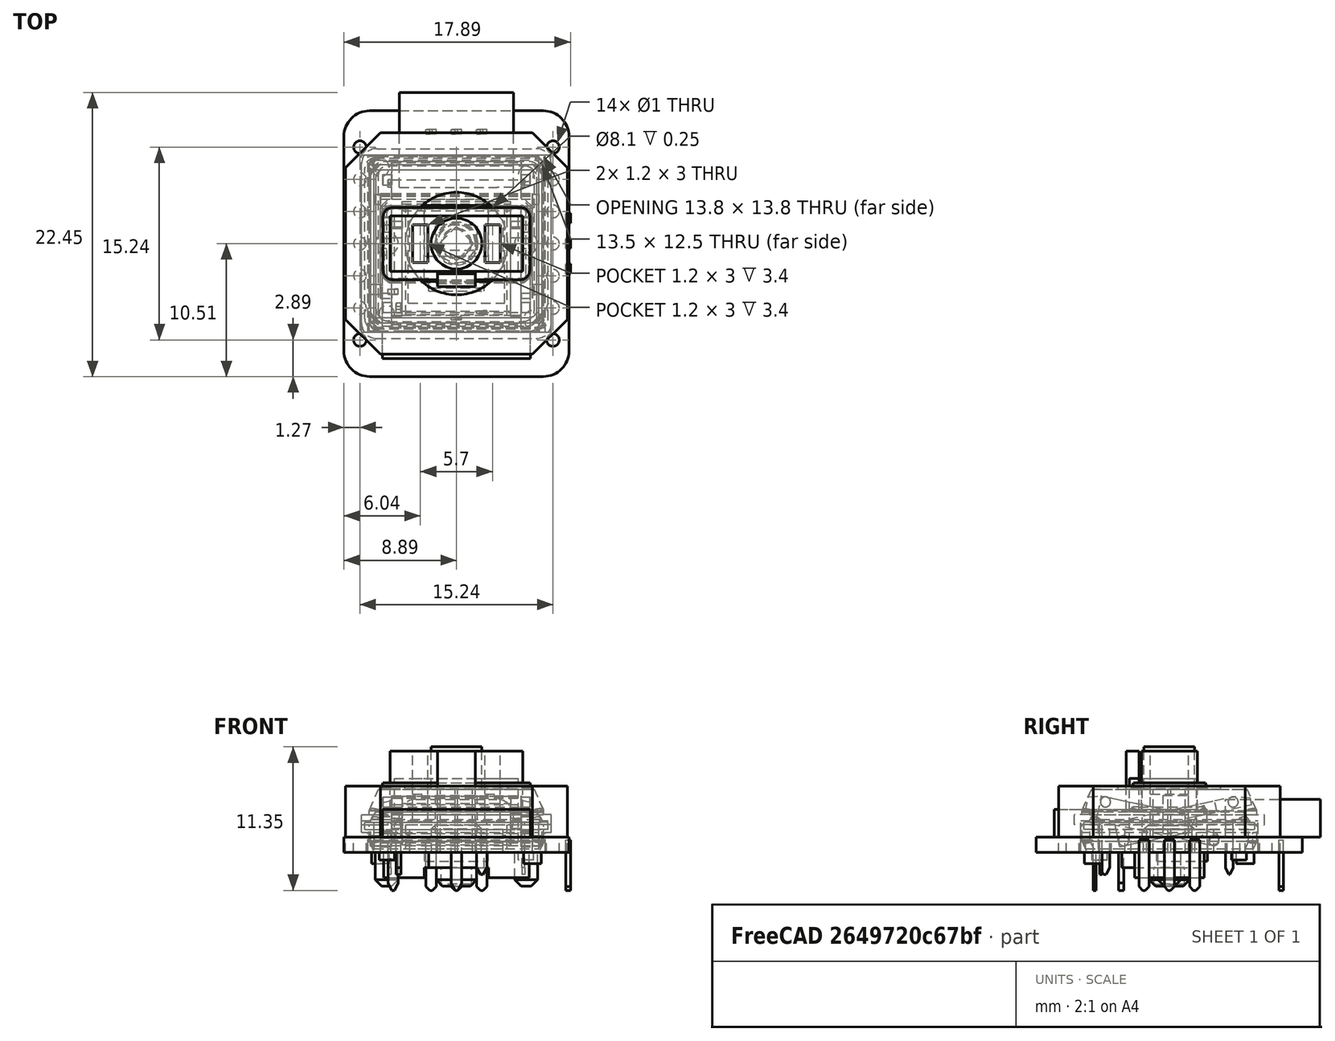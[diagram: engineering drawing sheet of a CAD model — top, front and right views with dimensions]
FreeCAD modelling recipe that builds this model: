
FCSTD DOCUMENT  (FreeCAD 0.18R)
Label: Keyboard
License: All rights reserved
LicenseURL: http://en.wikipedia.org/wiki/All_rights_reserved
objects: Part::Box×59, Part::Chamfer×31, Part::Cylinder×21, Part::MultiFuse×14, Part::Fillet×9, App::DocumentObjectGroup×6, Part::Cut×4, Part::FeaturePython×3
note: 141 computed .brp shape members not serialized (recipe doc carries the construction recipe); baked Part::Feature solids carry a one-line shape summary decoded from their .brp

FEATURE [Part::Box] Box  label="JT8P_Base"
  AttacherType = Attacher::AttachEngine3D
  Height = 5.25
  Length = 17.5
  Placement = pos=(-8.75,-8.75,0) rot=(0,0,1;0rad)
  Width = 17.5
FEATURE [Part::Cylinder] Cylinder  label="JT8P_TopHole"
  Angle = 360
  AttacherType = Attacher::AttachEngine3D
  Height = 2
  Placement = pos=(0,0,5) rot=(0,0,1;0rad)
  Radius = 4.05
FEATURE [Part::Cylinder] Cylinder001  label="JT8P_knob"
  Angle = 360
  AttacherType = Attacher::AttachEngine3D
  Height = 3.35
  Placement = pos=(0,0,5) rot=(0,0,1;0rad)
  Radius = 2
FEATURE [Part::Cylinder] Cylinder002  label="JT8P_Leg1"
  Angle = 360
  AttacherType = Attacher::AttachEngine3D
  Height = 0.9
  Placement = pos=(-6,6,-0.9) rot=(0,0,1;0rad)
  Radius = 0.7
FEATURE [Part::Cylinder] Cylinder003  label="JT8P_Leg2"
  Angle = 360
  AttacherType = Attacher::AttachEngine3D
  Height = 0.9
  Placement = pos=(6,-6,-0.9) rot=(0,0,1;0rad)
  Radius = 0.7
FEATURE [Part::Box] Box001  label="PG1350_BottomBase"
  AttacherType = Attacher::AttachEngine3D
  Height = 3
  Length = 13.8
  Placement = pos=(-6.9,-6.9,0) rot=(0,0,1;0rad)
  Width = 13.8
FEATURE [Part::Chamfer] Chamfer001  label="PG1350_BottomBase2"
  Base = -> Box001
  Edges = 4 edges: [Edge4 r1=0.9 r2=0.4,Edge8 r1=0.9 r2=0.4,Edge9 r1=0.9 r2=0.4,Edge11 r1=0.9 r2=0.4]
FEATURE [Part::Fillet] Fillet  label="PG1350_BottomBase3"
  Base = -> Chamfer001
  Edges = 8 edges: [Edge1 r=0.8,Edge4 r=0.8,Edge5 r=0.8,Edge8 r=0.8,Edge10 r=0.8,Edge13 r=0.8,Edge17 r=1,Edge20 r=0.8]
FEATURE [Part::Cylinder] Cylinder004  label="PG1350_LegCenter"
  Angle = 360
  AttacherType = Attacher::AttachEngine3D
  Height = 2.65
  Placement = pos=(0,0,-2.65) rot=(0,0,1;0rad)
  Radius = 1.6
FEATURE [Part::Box] Box002  label="PG1350_Fringe"
  AttacherType = Attacher::AttachEngine3D
  Height = 0.8
  Length = 15
  Placement = pos=(-7.5,-7.5,2.2) rot=(0,0,1;0rad)
  Width = 15
FEATURE [Part::Fillet] Fillet001  label="PG1350_Fringe2"
  Base = -> Box002
  Edges = 4 edges r=1.2: [Edge1,Edge3,Edge5,Edge7]
FEATURE [Part::Cylinder] Cylinder005  label="PG1350_Leg1"
  Angle = 360
  AttacherType = Attacher::AttachEngine3D
  Height = 2.65
  Placement = pos=(-5.5,0,-2.65) rot=(0,0,1;0rad)
  Radius = 0.9
FEATURE [Part::Cylinder] Cylinder006  label="PG1350_Leg2"
  Angle = 360
  AttacherType = Attacher::AttachEngine3D
  Height = 2.65
  Placement = pos=(5.5,0,-2.65) rot=(0,0,1;0rad)
  Radius = 0.9
FEATURE [Part::Box] Box003  label="PG1350_HullBase"
  AttacherType = Attacher::AttachEngine3D
  Height = 0.5
  Length = 11.9
  Placement = pos=(-5.95,-3,5) rot=(0,0,1;0rad)
  Width = 6
FEATURE [Part::Chamfer] Chamfer005  label="PG1350_Hull"
  Base = -> Box003
  Edges = 4 edges: [Edge2 r1=0.45 r2=0.15,Edge6 r1=0.45 r2=0.15,Edge10 r1=0.45 r2=0.15,Edge12 r1=0.45 r2=0.15]
FEATURE [Part::Fillet] Fillet002  label="PG1350_Hull2"
  Base = -> Chamfer005
  Edges = 8 edges r=0.8: [Edge1,Edge4,Edge5,Edge8,Edge10,Edge13,Edge17,Edge20]
FEATURE [Part::Box] Box004  label="PG1350_StemMain"
  AttacherType = Attacher::AttachEngine3D
  Height = 4.6
  Length = 10.5
  Placement = pos=(-5.25,-2.2,3.4) rot=(0,0,1;0rad)
  Width = 4.4
FEATURE [Part::Box] Box005  label="PG1350_StemSub"
  AttacherType = Attacher::AttachEngine3D
  Height = 4.6
  Length = 3
  Placement = pos=(-1.5,-3.4,3.4) rot=(0,0,1;0rad)
  Width = 1
FEATURE [Part::MultiFuse] Fusion  label="PG1350_StemBase"
  Shapes = -> [Box005,Box004]
FEATURE [Part::Box] Box006  label="PG1350_Hole1"
  AttacherType = Attacher::AttachEngine3D
  Height = 3.4
  Length = 1.2
  Placement = pos=(-3.45,-1.5,4.6) rot=(0,0,1;0rad)
  Width = 3
FEATURE [Part::Box] Box007  label="PG1350_Hole2"
  AttacherType = Attacher::AttachEngine3D
  Height = 3.4
  Length = 1.2
  Placement = pos=(2.25,-1.5,4.6) rot=(0,0,1;0rad)
  Width = 3
FEATURE [Part::MultiFuse] Fusion001  label="PG1350_Holes"
  Shapes = -> [Box007,Box006]
FEATURE [Part::Cut] Cut001  label="PG1350_Stem"
  Base = -> Fusion
  Tool = -> Fusion001
FEATURE [Part::Box] Box015  label="PG1232_BottomBase"
  AttacherType = Attacher::AttachEngine3D
  Height = 2.4
  Length = 13.5
  Placement = pos=(-6.75,-6.25,0) rot=(0,0,1;0rad)
  Width = 12.5
FEATURE [Part::Box] Box016  label="PG1232_FringeBase"
  AttacherType = Attacher::AttachEngine3D
  Height = 0.6
  Length = 14.5
  Placement = pos=(-7.25,-6.75,1.8) rot=(0,0,1;0rad)
  Width = 13.5
FEATURE [Part::Fillet] Fillet006  label="PG1232_Fringe"
  Base = -> Box016
  Edges = 4 edges r=0.8: [Edge1,Edge3,Edge5,Edge7]
FEATURE [Part::Chamfer] Chamfer011  label="PG1232_BottomBase2"
  Base = -> Box015
  Edges = 4 edges: [Edge4 r1=0.9 r2=0.4,Edge8 r1=0.9 r2=0.4,Edge9 r1=0.9 r2=0.4,Edge11 r1=0.9 r2=0.4]
FEATURE [Part::Box] Box017  label="PG1232_StemSub"
  AttacherType = Attacher::AttachEngine3D
  Height = 5
  Length = 3
  Placement = pos=(-1.5,-3.15,0.85) rot=(0,0,1;0rad)
  Width = 1
FEATURE [Part::Box] Box018  label="PG1232_StemMain"
  AttacherType = Attacher::AttachEngine3D
  Height = 5
  Length = 9.8
  Placement = pos=(-4.9,-2.15,0.85) rot=(0,0,1;0rad)
  Width = 4.3
FEATURE [Part::Box] Box019  label="PG1232_Hole1"
  AttacherType = Attacher::AttachEngine3D
  Height = 3.4
  Length = 1.2
  Placement = pos=(-3.45,-1.5,2.45) rot=(0,0,1;0rad)
  Width = 3
FEATURE [Part::Box] Box020  label="PG1232_Hole2"
  AttacherType = Attacher::AttachEngine3D
  Height = 3.4
  Length = 1.2
  Placement = pos=(2.25,-1.5,2.45) rot=(0,0,1;0rad)
  Width = 3
FEATURE [Part::MultiFuse] Fusion002  label="PG1232_Hole"
  Shapes = -> [Box020,Box019]
FEATURE [Part::MultiFuse] Fusion003  label="PG1232_StemBase"
  Shapes = -> [Box017,Box018]
FEATURE [Part::Cut] Cut002  label="PG1232_Stem"
  Base = -> Fusion003
  Tool = -> Fusion002
FEATURE [Part::Box] Box021  label="PG1232_Hull"
  AttacherType = Attacher::AttachEngine3D
  Height = 0.4
  Length = 11.4
  Placement = pos=(-5.7,-3.1,3.2) rot=(0,0,1;0rad)
  Width = 6.1
FEATURE [Part::Chamfer] Chamfer012  label="PG1232_Hull2"
  Base = -> Box021
  Edges = 4 edges: [Edge2 r1=0.3 r2=0.2,Edge6 r1=0.3 r2=0.2,Edge10 r1=0.3 r2=0.2,Edge12 r1=0.3 r2=0.2]
FEATURE [Part::Box] Box022  label="PG1232_PouchBase"
  AttacherType = Attacher::AttachEngine3D
  Height = 1.2
  Length = 5.1
  Placement = pos=(-2.55,-2.75,-1.2) rot=(0,0,1;0rad)
  Width = 5.5
FEATURE [Part::Cylinder] Cylinder007  label="PG1232_Cylinder"
  Angle = 360
  AttacherType = Attacher::AttachEngine3D
  Height = 1.3
  Placement = pos=(0,0,-2.5) rot=(0,0,1;0rad)
  Radius = 1.2
FEATURE [Part::Chamfer] Chamfer  label="JT8P_Base2"
  Base = -> Box
  Edges = 4 edges r=2.75: [Edge1,Edge3,Edge5,Edge7]
FEATURE [Part::Cut] Cut  label="JT8P_Base3"
  Base = -> Chamfer
  Tool = -> Cylinder
FEATURE [Part::Box] Box024  label="SKRHAAE010_Base"
  AttacherType = Attacher::AttachEngine3D
  Height = 1.8
  Length = 7.35
  Placement = pos=(-3.675,-3.5,0) rot=(0,0,1;0rad)
  Width = 7
FEATURE [Part::Chamfer] Chamfer013  label="SKRHAAE010_Base2"
  Base = -> Box024
  Edges = 4 edges r=1.7: [Edge1,Edge3,Edge5,Edge7]
FEATURE [Part::Cylinder] Cylinder008  label="SKRHAAE010_HullBase"
  Angle = 360
  AttacherType = Attacher::AttachEngine3D
  Height = 0.34
  Placement = pos=(0,0,1.8) rot=(0,0,1;0rad)
  Radius = 2
FEATURE [Part::Chamfer] Chamfer014  label="SKRHAAE010_Hull"
  Base = -> Cylinder008
  Edges = 1 edges r=0.3: [Edge1]
FEATURE [Part::Cylinder] Cylinder009  label="SKRHAAE010_KnobBase"
  Angle = 360
  AttacherType = Attacher::AttachEngine3D
  Height = 3
  Radius = 1.5
FEATURE [Part::Box] Box025  label="SKRHAAE010_Knob"
  AttacherType = Attacher::AttachEngine3D
  Height = 5
  Length = 1.95
  Placement = pos=(0,-1.37907,0) rot=(0,0,1;0.785398rad)
  Width = 1.95
  expr: Placement.Base.y = -1.95 / 1.4139999999999999
FEATURE [Part::Chamfer] Chamfer015  label="SKRHAAE010_Knob2"
  Base = -> Box025
  Edges = 4 edges r=0.15: [Edge1,Edge3,Edge5,Edge7]
FEATURE [App::DocumentObjectGroup] Group004  label="SKRHAAE010"
  Group = -> [Chamfer013,Chamfer014,Cylinder009,Chamfer015]
FEATURE [Part::MultiFuse] Fusion004  label="PG1350_LegsBase"
  Shapes = -> [Cylinder004,Cylinder005,Cylinder006]
FEATURE [Part::Chamfer] Chamfer016  label="PG1350_Legs"
  Base = -> Fusion004
  Edges = 3 edges r=0.5: [Edge3,Edge6,Edge9]
FEATURE [Part::Box] Box026  label="PG1350_TopBase"
  AttacherType = Attacher::AttachEngine3D
  Height = 2
  Length = 13.8
  Placement = pos=(-6.9,-6.9,3) rot=(0,0,1;0rad)
  Width = 13.8
FEATURE [Part::Chamfer] Chamfer017  label="PG1350_TopBase1"
  Base = -> Box026
  Edges = 4 edges: [Edge2 r1=1.7 r2=0.75,Edge6 r1=1.7 r2=0.75,Edge10 r1=1.7 r2=0.75,Edge12 r1=1.7 r2=0.75]
FEATURE [Part::Fillet] Fillet008  label="PG1350_TopBase2"
  Base = -> Chamfer017
  Edges = 8 edges: [Edge1 r=0.8,Edge4 r=0.8,Edge5 r=0.8,Edge8 r=0.8,Edge10 r=0.8,Edge13 r=0.8,Edge17 r=1,Edge20 r=0.8]
FEATURE [Part::MultiFuse] Fusion005  label="PG1350_Bottom"
  Shapes = -> [Fillet,Fillet001,Chamfer016]
FEATURE [Part::MultiFuse] Fusion006  label="PG1350_Top"
  Shapes = -> [Fillet008,Fillet002]
FEATURE [Part::Box] Box027  label="PG1232_TopBase"
  AttacherType = Attacher::AttachEngine3D
  Height = 0.8
  Length = 13.5
  Placement = pos=(-6.75,-6.25,2.4) rot=(0,0,1;0rad)
  Width = 12.5
FEATURE [Part::Chamfer] Chamfer018  label="PG1232_TopBase2"
  Base = -> Box027
  Edges = 4 edges: [Edge2 r1=0.6 r2=0.4,Edge6 r1=0.6 r2=0.4,Edge10 r1=0.6 r2=0.4,Edge12 r1=0.6 r2=0.4]
FEATURE [Part::Box] Box028  label="XIAO_Base"
  AttacherType = Attacher::AttachEngine3D
  Height = 1.2
  Length = 17.78
  Placement = pos=(-8.89,-10.508,0) rot=(0,0,1;0rad)
  Width = 20.9982
FEATURE [Part::Fillet] Fillet009  label="XIAO_Base2"
  Base = -> Box028
  Edges = 4 edges r=2.03: [Edge1,Edge3,Edge5,Edge7]
FEATURE [Part::Box] Box029  label="XIAO_TypeC"
  AttacherType = Attacher::AttachEngine3D
  Height = 3
  Length = 9
  Placement = pos=(-4.5,4.44,1.2) rot=(0,0,1;0rad)
  Width = 7.5
FEATURE [Part::Fillet] Fillet010  label="XIAO_TypeC2"
  Base = -> Box029
  Edges = 4 edges r=1.3: [Edge2,Edge4,Edge6,Edge8]
FEATURE [Part::Box] Box030  label="XIAO_Cover"
  AttacherType = Attacher::AttachEngine3D
  Height = 2.2
  Length = 11.7
  Placement = pos=(-5.85,-9.08,1.2) rot=(0,0,1;0rad)
  Width = 12.05
FEATURE [Part::Cylinder] Cylinder010  label="XIAO_TH"
  Angle = 360
  AttacherType = Attacher::AttachEngine3D
  Height = 2
  Placement = pos=(-7.62,-7.62,0) rot=(0,0,1;0rad)
  Radius = 0.5
FEATURE [Part::FeaturePython] Array  label="XIAO_TH_All"  # Draft array (typed FeaturePython)
  Angle = 360
  ArrayType = 0
  Axis = (0,0,1)
  Base = -> Cylinder010
  Center = (0,0,0)
  Fuse = false
  IntervalAxis = (0,0,0)
  IntervalX = (15.24,0,0)
  IntervalY = (0,2.54,0)
  IntervalZ = (0,0,1)
  NumberPolar = 1
  NumberX = 2
  NumberY = 7
  NumberZ = 1
FEATURE [Part::Cut] Cut004  label="XIAO_Base3"
  Base = -> Fillet009
  Tool = -> Array
FEATURE [App::DocumentObjectGroup] Group005  label="Seeeduino XIAO"
  Group = -> [Fillet010,Box030,Cut004]
FEATURE [Part::Box] Box031  label="PG1350_Pin1Base"
  AttacherType = Attacher::AttachEngine3D
  Height = 3
  Length = 0.8
  Placement = pos=(-0.4,-6,-3) rot=(0,0,1;0rad)
  Width = 0.2
FEATURE [Part::Box] Box032  label="PG1350_Pin2Base"
  AttacherType = Attacher::AttachEngine3D
  Height = 3
  Length = 0.8
  Placement = pos=(-5.4,-4,-3) rot=(0,0,1;0rad)
  Width = 0.4
FEATURE [Part::Chamfer] Chamfer019  label="PG1350_Pin1"
  Base = -> Box031
  Edges = 2 edges: [Edge4 r1=0.55 r2=0.3,Edge8 r1=0.55 r2=0.3]
FEATURE [Part::Chamfer] Chamfer020  label="PG1350_Pin2"
  Base = -> Box032
  Edges = 2 edges: [Edge4 r1=0.6 r2=0.3,Edge8 r1=0.6 r2=0.3]
FEATURE [App::DocumentObjectGroup] Group001  label="Kailh PG1350"
  Group = -> [Cut001,Fusion005,Fusion006,Chamfer019,Chamfer020]
FEATURE [Part::Box] Box033  label="PG1232_Pin1Base"
  AttacherType = Attacher::AttachEngine3D
  Height = 4.15
  Length = 0.8
  Placement = pos=(1.6,-5.51,-1.75) rot=(0,0,1;0rad)
  Width = 0.2
FEATURE [Part::Chamfer] Chamfer021  label="PG1232_Pin1"
  Base = -> Box033
  Edges = 2 edges: [Edge4 r1=0.55 r2=0.3,Edge8 r1=0.55 r2=0.3]
FEATURE [Part::Box] Box034  label="PG1232_Pin2Base"
  AttacherType = Attacher::AttachEngine3D
  Height = 4.15
  Length = 0.8
  Placement = pos=(-4.38,-5.5,-1.75) rot=(0,0,1;1.5708rad)
  Width = 0.4
FEATURE [Part::Chamfer] Chamfer022  label="PG1232_Pin2"
  Base = -> Box034
  Edges = 2 edges: [Edge4 r1=0.55 r2=0.3,Edge8 r1=0.55 r2=0.3]
FEATURE [Part::Box] Box035  label="PG1232_Pin3Base"
  AttacherType = Attacher::AttachEngine3D
  Height = 4.15
  Length = 0.6
  Placement = pos=(5.39,4.45,-1.75) rot=(0,0,1;1.5708rad)
  Width = 0.2
FEATURE [Part::Chamfer] Chamfer023  label="PG1232_Pin3"
  Base = -> Box035
  Edges = 2 edges: [Edge4 r1=0.55 r2=0.25,Edge8 r1=0.55 r2=0.25]
FEATURE [Part::Box] Box036  label="PG1232_Pin4Base"
  AttacherType = Attacher::AttachEngine3D
  Height = 4.15
  Length = 0.6
  Placement = pos=(-5.19,4.45,-1.75) rot=(0,0,1;1.5708rad)
  Width = 0.2
FEATURE [Part::Chamfer] Chamfer024  label="PG1232_Pin4"
  Base = -> Box036
  Edges = 2 edges: [Edge4 r1=0.55 r2=0.25,Edge8 r1=0.55 r2=0.25]
FEATURE [Part::Box] Box037  label="PG1232_PouchL"
  AttacherType = Attacher::AttachEngine3D
  Height = 2
  Length = 3.2
  Placement = pos=(-5.75,-2.75,-2) rot=(0,0,1;0rad)
  Width = 5.5
FEATURE [Part::Box] Box038  label="PG1232_PouchR"
  AttacherType = Attacher::AttachEngine3D
  Height = 2
  Length = 3.2
  Placement = pos=(2.55,-2.75,-2) rot=(0,0,1;0rad)
  Width = 5.5
FEATURE [Part::Box] Box023  label="PG1232_PouchSub"
  AttacherType = Attacher::AttachEngine3D
  Height = 1.2
  Length = 4.4
  Placement = pos=(-2.2,-3.75,-1.2) rot=(0,0,1;0rad)
  Width = 1
FEATURE [Part::MultiFuse] Fusion007  label="PG1232_Bottom"
  Shapes = -> [Cylinder007,Chamfer011,Fillet006,Box037,Box038,Box022,Box023]
FEATURE [Part::MultiFuse] Fusion009  label="PG1232_Pins"
  Shapes = -> [Chamfer024,Chamfer023,Chamfer022,Chamfer021]
FEATURE [Part::Fillet] Fillet007  label="PG1232_Hull3"
  Base = -> Chamfer012
  Edges = 8 edges r=0.6: [Edge1,Edge4,Edge5,Edge8,Edge10,Edge13,Edge17,Edge20]
FEATURE [Part::Fillet] Fillet011  label="PG1232_TopBase3"
  Base = -> Chamfer018
  Edges = 8 edges r=0.8: [Edge1,Edge4,Edge5,Edge8,Edge10,Edge13,Edge17,Edge20]
FEATURE [Part::MultiFuse] Fusion008  label="PG1232_Top"
  Shapes = -> [Fillet007,Fillet011]
FEATURE [App::DocumentObjectGroup] Group003  label="Kailh PG1232"
  Group = -> [Cut002,Fusion007,Fusion008,Fusion009]
FEATURE [Part::Box] Box039  label="JT8P_PinBase"
  AttacherType = Attacher::AttachEngine3D
  Height = 4
  Length = 0.35
  Placement = pos=(8.65,-2.4,-3) rot=(0,0,1;0rad)
  Width = 0.8
FEATURE [Part::MultiFuse] Fusion010  label="JT8P_Body"
  Shapes = -> [Cut,Cylinder003,Cylinder002,Cylinder001]
FEATURE [Part::Chamfer] Chamfer025  label="JT8P_Pin"
  Base = -> Box039
  Edges = 2 edges r=0.3: [Edge9,Edge11]
FEATURE [Part::FeaturePython] Array001  label="JT8P_PinsSide1"  # Draft array (typed FeaturePython)
  Angle = 90
  ArrayType = 0
  Axis = (0,0,1)
  Base = -> Chamfer025
  Center = (0,0,0)
  Fuse = false
  IntervalAxis = (0,8,0)
  IntervalX = (2,0,0)
  IntervalY = (0,2,0)
  IntervalZ = (0,0,1)
  NumberPolar = 1
  NumberX = 1
  NumberY = 3
  NumberZ = 1
FEATURE [Part::FeaturePython] Array002  label="JT8P_Pins"  # Draft array (typed FeaturePython)
  Angle = 90
  ArrayType = 1
  Axis = (0,0,1)
  Base = -> Array001
  Center = (0,0,0)
  Fuse = false
  IntervalAxis = (0,0,0)
  IntervalX = (1,0,0)
  IntervalY = (0,1,0)
  IntervalZ = (0,0,1)
  NumberPolar = 2
  NumberX = 0
  NumberY = 0
  NumberZ = 0
FEATURE [App::DocumentObjectGroup] Group  label="JT8P"
  Group = -> [Fusion010,Array002]
FEATURE [Part::Box] Box040  label="PG1425_BottomBase"
  AttacherType = Attacher::AttachEngine3D
  Height = 0.3
  Length = 14
  Placement = pos=(-7,-7,0) rot=(0,0,1;0rad)
  Width = 14
FEATURE [Part::Box] Box041  label="PG1425_Left001"
  AttacherType = Attacher::AttachEngine3D
  Height = 1.3
  Length = 0.5
  Placement = pos=(-7,-7,0.3) rot=(0,0,1;0rad)
  Width = 14
FEATURE [Part::Box] Box042  label="PG1425_Right001"
  AttacherType = Attacher::AttachEngine3D
  Height = 1.3
  Length = 0.5
  Placement = pos=(6.5,-7,0.3) rot=(0,0,1;0rad)
  Width = 14
FEATURE [Part::Box] Box043  label="PG1425_Left002"
  AttacherType = Attacher::AttachEngine3D
  Height = 0.9
  Length = 1
  Placement = pos=(-7.5,-7,1.6) rot=(0,0,1;0rad)
  Width = 14
FEATURE [Part::Box] Box044  label="PG1425_Right002"
  AttacherType = Attacher::AttachEngine3D
  Height = 0.9
  Length = 1
  Placement = pos=(6.5,-7,1.6) rot=(0,0,1;0rad)
  Width = 14
FEATURE [Part::Box] Box045  label="PG1425_Back"
  AttacherType = Attacher::AttachEngine3D
  Height = 1.3
  Length = 13
  Placement = pos=(-6.5,6.6,0.3) rot=(0,0,1;0rad)
  Width = 0.4
FEATURE [Part::Box] Box046  label="PG1425_Front"
  AttacherType = Attacher::AttachEngine3D
  Height = 0.7
  Length = 13
  Placement = pos=(-6.5,-7,0.3) rot=(0,0,1;0rad)
  Width = 0.4
FEATURE [Part::Box] Box047  label="PG1425_BottomStem"
  AttacherType = Attacher::AttachEngine3D
  Height = 0.7
  Length = 5
  Placement = pos=(-2.5,-1,-0.7) rot=(0,0,1;0rad)
  Width = 4
FEATURE [Part::Box] Box048  label="PG1425_TopPlate"
  AttacherType = Attacher::AttachEngine3D
  Height = 0.1
  Length = 7.6
  Placement = pos=(-3.8,-4.7,2.4) rot=(0,0,1;0rad)
  Width = 7.7
FEATURE [Part::Cylinder] Cylinder011  label="PG1425_Leg1"
  Angle = 360
  AttacherType = Attacher::AttachEngine3D
  Height = 0.6
  Placement = pos=(-5.5,-5.5,-0.6) rot=(0,0,1;0rad)
  Radius = 0.6
FEATURE [Part::Cylinder] Cylinder012  label="PG1425_Leg2"
  Angle = 360
  AttacherType = Attacher::AttachEngine3D
  Height = 0.6
  Placement = pos=(5.5,5.5,-0.6) rot=(0,0,1;0rad)
  Radius = 0.6
FEATURE [Part::Box] Box049  label="PG1425_Stem"
  AttacherType = Attacher::AttachEngine3D
  Height = 3
  Length = 3.3
  Placement = pos=(-1.65,-0.5,1.5) rot=(0,0,1;0rad)
  Width = 2
FEATURE [Part::Box] Box050  label="PG1425_BackShaft001"
  AttacherType = Attacher::AttachEngine3D
  Height = 0.9
  Length = 10.2
  Placement = pos=(-5.1,3.2,1.6) rot=(0,0,1;0rad)
  Width = 3.8
FEATURE [Part::Box] Box051  label="PG1425_BackShaft002"
  AttacherType = Attacher::AttachEngine3D
  Height = 0.9
  Length = 0.9
  Placement = pos=(-6,-3.9,1.6) rot=(0,0,1;0rad)
  Width = 8.1
FEATURE [Part::Box] Box052  label="PG1425_BackShaft003"
  AttacherType = Attacher::AttachEngine3D
  Height = 0.9
  Length = 0.9
  Placement = pos=(5.1,-3.9,1.6) rot=(0,0,1;0rad)
  Width = 8.1
FEATURE [Part::Box] Box053  label="PG1425_BackShaft004"
  AttacherType = Attacher::AttachEngine3D
  Height = 0.9
  Length = 0.8
  Placement = pos=(-5.1,1,1.6) rot=(0,0,1;0rad)
  Width = 2.2
FEATURE [Part::Box] Box054  label="PG1425_BackShaft005"
  AttacherType = Attacher::AttachEngine3D
  Height = 0.9
  Length = 0.8
  Placement = pos=(4.3,1,1.6) rot=(0,0,1;0rad)
  Width = 2.2
FEATURE [Part::Box] Box055  label="PG1425_TopStem"
  AttacherType = Attacher::AttachEngine3D
  Height = 2.1
  Length = 8
  Placement = pos=(-4,-5.6,0.3) rot=(0,0,1;0rad)
  Width = 8.6
FEATURE [Part::MultiFuse] Fusion011  label="PG1425_Bottom"
  Shapes = -> [Box047,Box046,Box045,Box044,Box043,Box042,Box041,Box040,Cylinder011,Cylinder012,Box055]
FEATURE [Part::Box] Box056  label="PG1425_FrontShaft001"
  AttacherType = Attacher::AttachEngine3D
  Height = 1.5
  Length = 10.2
  Placement = pos=(-5.1,-7,1) rot=(0,0,1;0rad)
  Width = 1
FEATURE [Part::Box] Box057  label="PG1425_FrontShaft003"
  AttacherType = Attacher::AttachEngine3D
  Height = 2
  Length = 0.8
  Placement = pos=(4.3,-6,0.5) rot=(0,0,1;0rad)
  Width = 7.5
FEATURE [Part::Box] Box058  label="PG1425_FrontShaft002"
  AttacherType = Attacher::AttachEngine3D
  Height = 2
  Length = 0.8
  Placement = pos=(-5.1,-6,0.5) rot=(0,0,1;0rad)
  Width = 7.5
FEATURE [Part::Box] Box059  label="PG1425_FrontShaft004"
  AttacherType = Attacher::AttachEngine3D
  Height = 1
  Length = 0.8
  Placement = pos=(-5.1,1.5,0.5) rot=(0,0,1;0rad)
  Width = 1.6
FEATURE [Part::Box] Box060  label="PG1425_FrontShaft005"
  AttacherType = Attacher::AttachEngine3D
  Height = 1
  Length = 0.8
  Placement = pos=(4.3,1.5,0.5) rot=(0,0,1;0rad)
  Width = 1.6
FEATURE [Part::Box] Box061  label="PG1425_FrontShaft006"
  AttacherType = Attacher::AttachEngine3D
  Height = 1
  Length = 10.2
  Placement = pos=(-5.1,3.1,0.5) rot=(0,0,1;0rad)
  Width = 0.7
FEATURE [Part::Box] Box062  label="PG1425_BackShaft006"
  AttacherType = Attacher::AttachEngine3D
  Height = 1.1
  Length = 0.9
  Placement = pos=(-6,-3.9,0.5) rot=(0,0,1;0rad)
  Width = 6.4
FEATURE [Part::Box] Box063  label="PG1425_BackShaft007"
  AttacherType = Attacher::AttachEngine3D
  Height = 1.1
  Length = 0.9
  Placement = pos=(5.1,-3.9,0.5) rot=(0,0,1;0rad)
  Width = 6.4
FEATURE [Part::Chamfer] Chamfer028  label="PG1425_FrontShaftCham001"
  Base = -> Box056
  Edges = 1 edges: [Edge10 r1=0.3 r2=0.9]
FEATURE [Part::Chamfer] Chamfer029  label="PG1425_FrontShaftCham002"
  Base = -> Box058
  Edges = 1 edges: [Edge12 r1=1 r2=0.8]
FEATURE [Part::Chamfer] Chamfer030  label="PG1425_FrontShaftCham003"
  Base = -> Box057
  Edges = 1 edges: [Edge12 r1=1 r2=0.8]
FEATURE [Part::Chamfer] Chamfer033  label="PG1425_FrontShaftCham006"
  Base = -> Box061
  Edges = 2 edges r=0.3: [Edge11,Edge12]
FEATURE [Part::Cylinder] Cylinder013  label="PG1425_FrontShaft009"
  Angle = 360
  AttacherType = Attacher::AttachEngine3D
  Height = 0.5
  Placement = pos=(-6.5,3.4,0.9) rot=(0,1,0;1.5708rad)
  Radius = 0.4
FEATURE [Part::Cylinder] Cylinder014  label="PG1425_FrontShaft010"
  Angle = 360
  AttacherType = Attacher::AttachEngine3D
  Height = 0.5
  Placement = pos=(6,3.4,0.9) rot=(0,1,0;1.5708rad)
  Radius = 0.4
FEATURE [Part::Cylinder] Cylinder015  label="PG1425_FrontShaft011"
  Angle = 360
  AttacherType = Attacher::AttachEngine3D
  Height = 0.7
  Placement = pos=(-5.8,-5.6,2.1) rot=(0,1,0;1.5708rad)
  Radius = 0.4
FEATURE [Part::Cylinder] Cylinder016  label="PG1425_FrontShaft012"
  Angle = 360
  AttacherType = Attacher::AttachEngine3D
  Height = 0.7
  Placement = pos=(5.1,-5.6,2.1) rot=(0,1,0;1.5708rad)
  Radius = 0.4
FEATURE [Part::Chamfer] Chamfer034  label="PG1425_BackShaftCham001"
  Base = -> Box050
  Edges = 1 edges: [Edge12 r1=0.4 r2=1.3]
FEATURE [Part::Chamfer] Chamfer035  label="PG1425_BackShaftCham002"
  Base = -> Box051
  Edges = 1 edges r=0.89: [Edge3]
FEATURE [Part::Chamfer] Chamfer036  label="PG1425_BackShaftCham003"
  Base = -> Box052
  Edges = 1 edges r=0.89: [Edge7]
FEATURE [Part::Chamfer] Chamfer037  label="PG1425_BackShaftCham004"
  Base = -> Box053
  Edges = 1 edges: [Edge9 r1=0.89 r2=0.71]
FEATURE [Part::Chamfer] Chamfer038  label="PG1425_BackShaftCham005"
  Base = -> Box054
  Edges = 1 edges: [Edge9 r1=0.89 r2=0.71]
FEATURE [Part::Chamfer] Chamfer039  label="PG1425_BackShaftCham006"
  Base = -> Box062
  Edges = 1 edges: [Edge11 r1=1.09 r2=0.87]
FEATURE [Part::Chamfer] Chamfer040  label="PG1425_BackShaftCham007"
  Base = -> Box063
  Edges = 1 edges: [Edge11 r1=1.09 r2=0.87]
FEATURE [Part::Cylinder] Cylinder017  label="PG1425_BackShaft008"
  Angle = 360
  AttacherType = Attacher::AttachEngine3D
  Height = 0.8
  Placement = pos=(-6.8,-3.5,0.9) rot=(0,1,0;1.5708rad)
  Radius = 0.4
FEATURE [Part::Cylinder] Cylinder018  label="PG1425_BackShaft009"
  Angle = 360
  AttacherType = Attacher::AttachEngine3D
  Height = 0.8
  Placement = pos=(6,-3.5,0.9) rot=(0,1,0;1.5708rad)
  Radius = 0.4
FEATURE [Part::Cylinder] Cylinder019  label="PG1425_BackShaft010"
  Angle = 360
  AttacherType = Attacher::AttachEngine3D
  Height = 0.7
  Placement = pos=(-5.8,5.6,2.1) rot=(0,1,0;1.5708rad)
  Radius = 0.4
FEATURE [Part::Cylinder] Cylinder020  label="PG1425_BackShaft011"
  Angle = 360
  AttacherType = Attacher::AttachEngine3D
  Height = 0.7
  Placement = pos=(5.1,5.6,2.1) rot=(0,1,0;1.5708rad)
  Radius = 0.4
FEATURE [Part::MultiFuse] Fusion015  label="PG1425_BackShaft"
  Placement = pos=(0,0,0.769273) rot=(1,0,0;0.20944rad)
  Shapes = -> [Chamfer034,Chamfer035,Chamfer036,Chamfer037,Chamfer038,Chamfer039,Chamfer040,Cylinder017,Cylinder018,Cylinder019,Cylinder020]
  expr: Placement.Base.z = 37mm * sin(Placement.Rotation.Angle) / 10
FEATURE [Part::Box] Box064  label="PG1425_FrontShaft008"
  AttacherType = Attacher::AttachEngine3D
  Height = 1
  Length = 0.9
  Placement = pos=(5.1,2,0.5) rot=(0,0,1;0rad)
  Width = 1.8
FEATURE [Part::Chamfer] Chamfer042  label="PG1425_FrontShaftCham008"
  Base = -> Box064
  Edges = 3 edges: [Edge10 r1=0.9 r2=0.72,Edge11 r=0.3,Edge12 r=0.3]
FEATURE [Part::Box] Box065  label="PG1425_FrontShaft007"
  AttacherType = Attacher::AttachEngine3D
  Height = 1
  Length = 0.9
  Placement = pos=(-6,2,0.5) rot=(0,0,1;0rad)
  Width = 1.8
FEATURE [Part::Chamfer] Chamfer041  label="PG1425_FrontShaftCham007"
  Base = -> Box065
  Edges = 3 edges: [Edge10 r1=0.9 r2=0.72,Edge11 r=0.3,Edge12 r=0.3]
FEATURE [Part::MultiFuse] Fusion014  label="PG1425_FrontShaft"
  Placement = pos=(0,0,0.769273) rot=(-1,0,0;0.20944rad)
  Shapes = -> [Chamfer028,Chamfer029,Chamfer030,Chamfer033,Cylinder013,Cylinder014,Cylinder015,Cylinder016,Box059,Box060,Chamfer041,Chamfer042]
  expr: Placement.Base.z = 37mm * sin(Placement.Rotation.Angle) / 10
FEATURE [App::DocumentObjectGroup] Group006  label="Kailh_PG1425"
  Group = -> [Fusion011,Box048,Box049,Fusion014,Fusion015]
